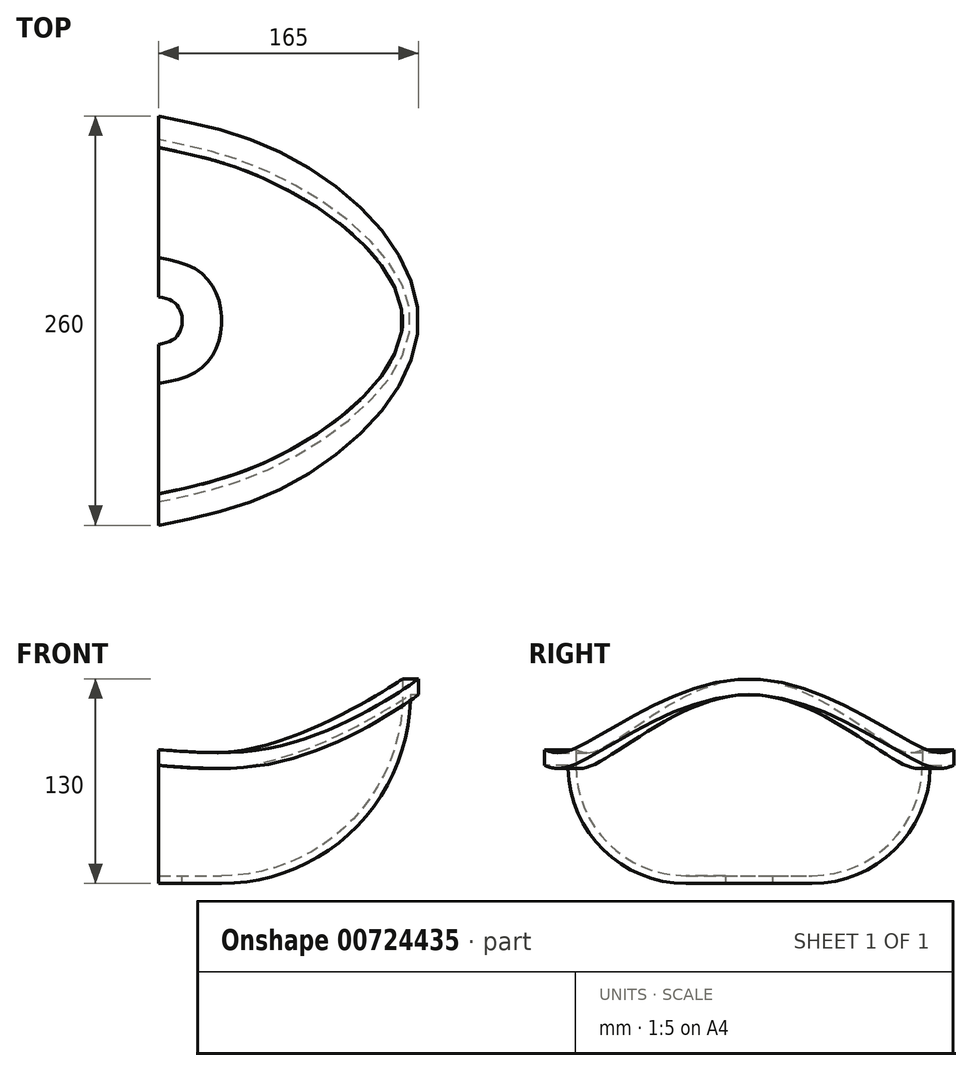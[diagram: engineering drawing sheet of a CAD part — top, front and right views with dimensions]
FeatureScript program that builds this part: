
annotation { "Feature Type Name" : "Feature", "Feature Type Description" : "" }
export const myFeature = defineFeature(function(context is Context, id is Id, definition is map)
    precondition{}
    {
        {
            var Q0;
            Q0=qCreatedBy(makeId("Front.planeOp"),FACE);
            var sketch = newSketch(context, id + "F0", { "sketchPlane" : qUnion([Q0])});
            skLineSegment(sketch, "E0.bottom", {"start": v(15, 5) * mm, "end": v(40, 5) * mm});
            skLineSegment(sketch, "E0.top", {"start": v(15, 0) * mm, "end": v(40, 0) * mm});
            skLineSegment(sketch, "E0.left", {"start": v(15, 5) * mm, "end": v(15, 0) * mm});
            skLineSegment(sketch, "E0.right", {"start": v(40, 5) * mm, "end": v(40, 0) * mm, "construction": true});
            skLineSegment(sketch, "E1.bottom", {"start": v(155, 130) * mm, "end": v(165, 130) * mm});
            skLineSegment(sketch, "E1.top", {"start": v(160, 120) * mm, "end": v(165, 120) * mm});
            skLineSegment(sketch, "E1.left", {"start": v(155, 130) * mm, "end": v(155, 120) * mm});
            skLineSegment(sketch, "E1.right", {"start": v(165, 130) * mm, "end": v(165, 120) * mm});
            skArc(sketch, "E2", {"start": v(40, 0) * mm, "mid": v(124.85, 35.15) * mm, "end": v(160, 120) * mm});
            skArc(sketch, "E3", {"start": v(40, 5) * mm, "mid": v(121.32, 38.68) * mm, "end": v(155, 120) * mm});
            skLineSegment(sketch, "E4", {"start": v(0, 0) * mm, "end": v(0, 50) * mm, "construction": true});
            skSolve(sketch);
        }
        {
            var Q0;
            Q0=sQuery(id+"F0.wireOp",EDGE,"E4");
            cPlane(context, id + "F1", {"entities" : qUnion([Q0]), "cplaneType" : CPlaneType.LINE_ANGLE, "offset" : 25 * mm, "angle" : 30 * degree, "oppositeDirection" : true, "width" : 150 * mm, "height" : 150 * mm});
        }
        {
            var Q0;
            Q0=qCreatedBy(id+"F1.planeOp",FACE);
            var sketch = newSketch(context, id + "F2", { "sketchPlane" : qUnion([Q0])});
            skLineSegment(sketch, "E5.bottom", {"start": v(15, 5) * mm, "end": v(40, 5) * mm});
            skLineSegment(sketch, "E5.top", {"start": v(15, 0) * mm, "end": v(40, 0) * mm});
            skLineSegment(sketch, "E5.left", {"start": v(15, 5) * mm, "end": v(15, 0) * mm});
            skLineSegment(sketch, "E5.right", {"start": v(40, 5) * mm, "end": v(40, 0) * mm, "construction": true});
            skLineSegment(sketch, "E6.bottom", {"start": v(110, 85) * mm, "end": v(130, 85) * mm});
            skLineSegment(sketch, "E6.top", {"start": v(115, 75) * mm, "end": v(130, 75) * mm});
            skLineSegment(sketch, "E6.left", {"start": v(110, 85) * mm, "end": v(110, 75) * mm});
            skLineSegment(sketch, "E6.right", {"start": v(130, 85) * mm, "end": v(130, 75) * mm});
            skArc(sketch, "E7", {"start": v(40, 0) * mm, "mid": v(93.03, 21.97) * mm, "end": v(115, 75) * mm});
            skArc(sketch, "E8", {"start": v(40, 5) * mm, "mid": v(89.5, 25.5) * mm, "end": v(110, 75) * mm});
            skLineSegment(sketch, "E9", {"start": v(0, 0) * mm, "end": v(0, 50) * mm, "construction": true});
            skSolve(sketch);
        }
        {
            var Q0;
            Q0=sQuery(id+"F0.wireOp",EDGE,"E4");
            cPlane(context, id + "F3", {"entities" : qUnion([Q0]), "cplaneType" : CPlaneType.LINE_ANGLE, "offset" : 25 * mm, "angle" : 150 * degree, "oppositeDirection" : true, "width" : 150 * mm, "height" : 150 * mm});
        }
        {
            var Q0;
            Q0=qCreatedBy(id+"F3.planeOp",FACE);
            var sketch = newSketch(context, id + "F4", { "sketchPlane" : qUnion([Q0])});
            skLineSegment(sketch, "E10.bottom", {"start": v(15, 5) * mm, "end": v(40, 5) * mm});
            skLineSegment(sketch, "E10.top", {"start": v(15, 0) * mm, "end": v(40, 0) * mm});
            skLineSegment(sketch, "E10.left", {"start": v(15, 5) * mm, "end": v(15, 0) * mm});
            skLineSegment(sketch, "E10.right", {"start": v(40, 5) * mm, "end": v(40, 0) * mm, "construction": true});
            skLineSegment(sketch, "E11.bottom", {"start": v(110, 85) * mm, "end": v(130, 85) * mm});
            skLineSegment(sketch, "E11.top", {"start": v(115, 75) * mm, "end": v(130, 75) * mm});
            skLineSegment(sketch, "E11.left", {"start": v(110, 85) * mm, "end": v(110, 75) * mm});
            skLineSegment(sketch, "E11.right", {"start": v(130, 85) * mm, "end": v(130, 75) * mm});
            skArc(sketch, "E12", {"start": v(40, 0) * mm, "mid": v(93.03, 21.97) * mm, "end": v(115, 75) * mm});
            skArc(sketch, "E13", {"start": v(40, 5) * mm, "mid": v(89.5, 25.5) * mm, "end": v(110, 75) * mm});
            skLineSegment(sketch, "E14", {"start": v(0, 0) * mm, "end": v(0, 50) * mm, "construction": true});
            skSolve(sketch);
        }
        {
            var Q0;
            Q0=qCreatedBy(makeId("Right.planeOp"),FACE);
            var sketch = newSketch(context, id + "F5", { "sketchPlane" : qUnion([Q0])});
            skLineSegment(sketch, "E15.bottom", {"start": v(15, 5) * mm, "end": v(40, 5) * mm});
            skLineSegment(sketch, "E15.top", {"start": v(15, 0) * mm, "end": v(40, 0) * mm});
            skLineSegment(sketch, "E15.left", {"start": v(15, 5) * mm, "end": v(15, 0) * mm});
            skLineSegment(sketch, "E15.right", {"start": v(40, 5) * mm, "end": v(40, 0) * mm, "construction": true});
            skLineSegment(sketch, "E16.bottom", {"start": v(110, 85) * mm, "end": v(130, 85) * mm});
            skLineSegment(sketch, "E16.top", {"start": v(115, 75) * mm, "end": v(130, 75) * mm});
            skLineSegment(sketch, "E16.left", {"start": v(110, 85) * mm, "end": v(110, 75) * mm});
            skLineSegment(sketch, "E16.right", {"start": v(130, 85) * mm, "end": v(130, 75) * mm});
            skArc(sketch, "E17", {"start": v(40, 0) * mm, "mid": v(93.03, 21.97) * mm, "end": v(115, 75) * mm});
            skArc(sketch, "E18", {"start": v(40, 5) * mm, "mid": v(89.5, 25.5) * mm, "end": v(110, 75) * mm});
            skLineSegment(sketch, "E19", {"start": v(0, 0) * mm, "end": v(0, 50) * mm, "construction": true});
            skSolve(sketch);
        }
        {
            var Q0;
            Q0=sQuery(id+"F5.wireOp",EDGE,"E19");
            cPlane(context, id + "F6", {"entities" : qUnion([Q0]), "cplaneType" : CPlaneType.LINE_ANGLE, "offset" : 25 * mm, "angle" : 180 * degree, "width" : 150 * mm, "height" : 150 * mm});
        }
        {
            var Q0;
            Q0=qCreatedBy(id+"F6.planeOp",FACE);
            var sketch = newSketch(context, id + "F7", { "sketchPlane" : qUnion([Q0])});
            skLineSegment(sketch, "E20.bottom", {"start": v(15, 5) * mm, "end": v(40, 5) * mm});
            skLineSegment(sketch, "E20.top", {"start": v(15, 0) * mm, "end": v(40, 0) * mm});
            skLineSegment(sketch, "E20.left", {"start": v(15, 5) * mm, "end": v(15, 0) * mm});
            skLineSegment(sketch, "E20.right", {"start": v(40, 5) * mm, "end": v(40, 0) * mm, "construction": true});
            skLineSegment(sketch, "E21.bottom", {"start": v(110, 85) * mm, "end": v(130, 85) * mm});
            skLineSegment(sketch, "E21.top", {"start": v(115, 75) * mm, "end": v(130, 75) * mm});
            skLineSegment(sketch, "E21.left", {"start": v(110, 85) * mm, "end": v(110, 75) * mm});
            skLineSegment(sketch, "E21.right", {"start": v(130, 85) * mm, "end": v(130, 75) * mm});
            skArc(sketch, "E22", {"start": v(40, 0) * mm, "mid": v(93.03, 21.97) * mm, "end": v(115, 75) * mm});
            skArc(sketch, "E23", {"start": v(40, 5) * mm, "mid": v(89.5, 25.5) * mm, "end": v(110, 75) * mm});
            skLineSegment(sketch, "E24", {"start": v(0, 0) * mm, "end": v(0, 50) * mm, "construction": true});
            skSolve(sketch);
        }
        {
            var Q0;
            Q0=makeQuery(id+"F7.imprint","IMPRINT",FACE,{"disambiguationData":[TD([[makeQuery(id+"F7.imprint","IMPRINT",EDGE,{"derivedFrom":sQuery(id+"F7.wireOp",EDGE,"E20.bottom")}),-1.0]])]});
            var Q1;
            Q1=makeQuery(id+"F4.imprint","IMPRINT",FACE,{"disambiguationData":[TD([[makeQuery(id+"F4.imprint","IMPRINT",EDGE,{"derivedFrom":sQuery(id+"F4.wireOp",EDGE,"E10.bottom")}),-1.0]])]});
            var Q2;
            Q2=makeQuery(id+"F0.imprint","IMPRINT",FACE,{"disambiguationData":[TD([[makeQuery(id+"F0.imprint","IMPRINT",EDGE,{"derivedFrom":sQuery(id+"F0.wireOp",EDGE,"E0.bottom")}),-1.0]])]});
            var Q3;
            Q3=makeQuery(id+"F2.imprint","IMPRINT",FACE,{"disambiguationData":[TD([[makeQuery(id+"F2.imprint","IMPRINT",EDGE,{"derivedFrom":sQuery(id+"F2.wireOp",EDGE,"E5.bottom")}),-1.0]])]});
            var Q4;
            Q4=makeQuery(id+"F5.imprint","IMPRINT",FACE,{"disambiguationData":[TD([[makeQuery(id+"F5.imprint","IMPRINT",EDGE,{"derivedFrom":sQuery(id+"F5.wireOp",EDGE,"E15.bottom")}),-1.0]])]});
            loft(context, id + "F8", {"sheetProfilesArray" : [{ "sheetProfileEntities" : qUnion([Q0]) }, { "sheetProfileEntities" : qUnion([Q1]) }, { "sheetProfileEntities" : qUnion([Q2]) }, { "sheetProfileEntities" : qUnion([Q3]) }, { "sheetProfileEntities" : qUnion([Q4]) }]});
        }
    });
